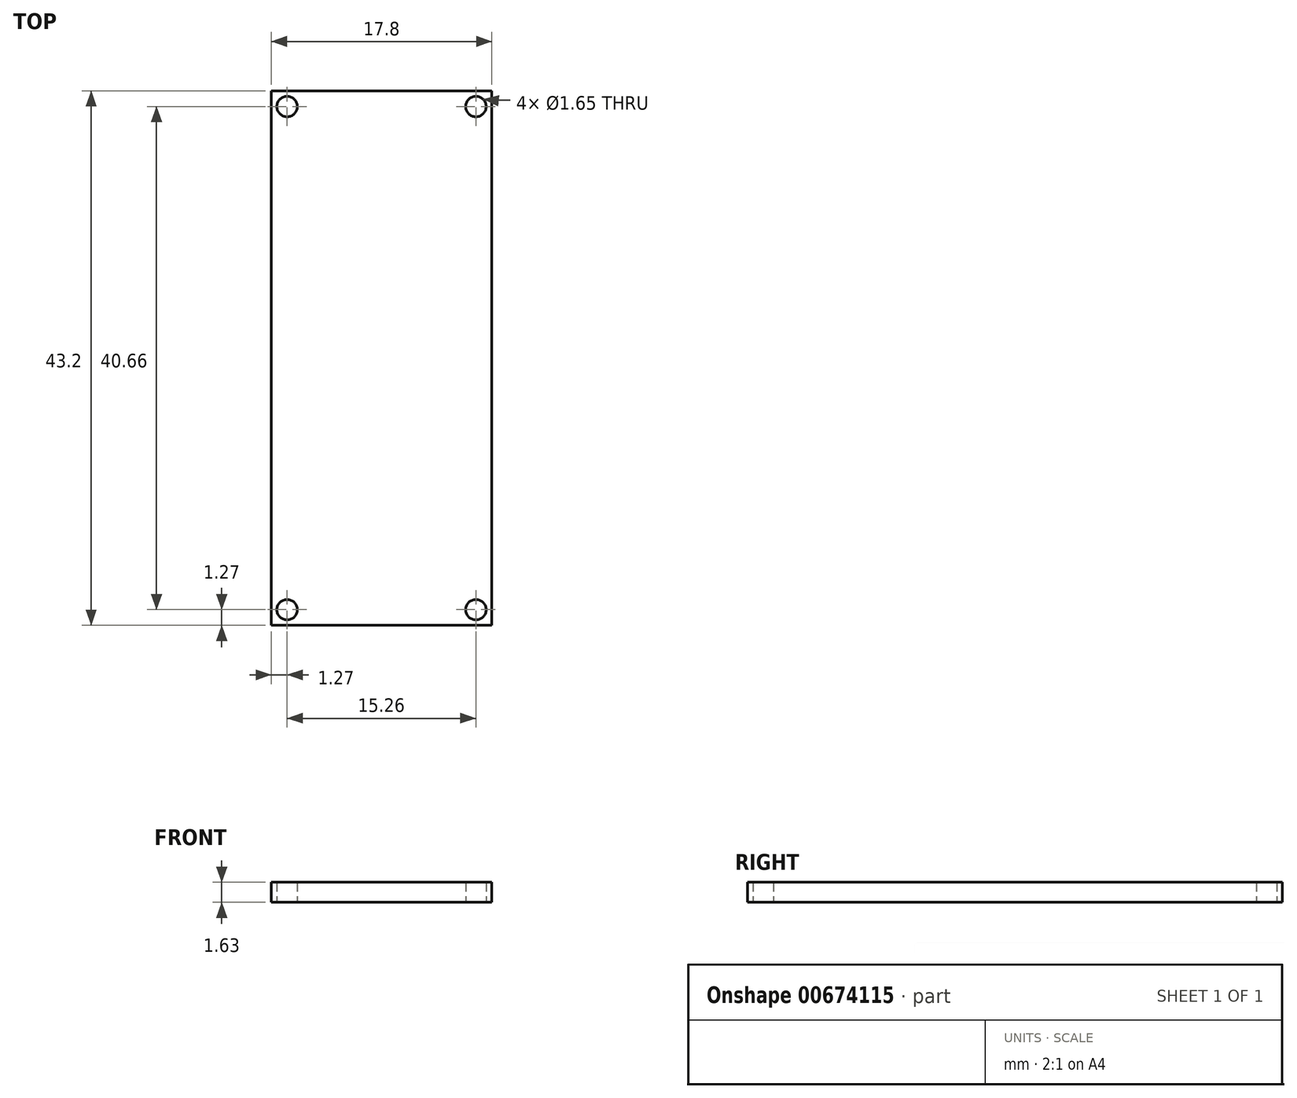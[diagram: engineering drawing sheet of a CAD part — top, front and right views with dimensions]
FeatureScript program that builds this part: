
annotation { "Feature Type Name" : "Feature", "Feature Type Description" : "" }
export const myFeature = defineFeature(function(context is Context, id is Id, definition is map)
    precondition{}
    {
        {
            var Q0;
            Q0=qCreatedBy(makeId("Top.planeOp"),FACE);
            var sketch = newSketch(context, id + "F0", { "sketchPlane" : qUnion([Q0])});
            skLineSegment(sketch, "E0.bottom", {"start": v(8.9, 21.6) * mm, "end": v(-8.9, 21.6) * mm});
            skLineSegment(sketch, "E0.top", {"start": v(8.9, -21.6) * mm, "end": v(-8.9, -21.6) * mm});
            skLineSegment(sketch, "E0.left", {"start": v(8.9, 21.6) * mm, "end": v(8.9, -21.6) * mm});
            skLineSegment(sketch, "E0.right", {"start": v(-8.9, 21.6) * mm, "end": v(-8.9, -21.6) * mm});
            skPoint(sketch, "E0.middle", {"position": v(0, 0) * mm});
            skCircle(sketch, "E1", {"center": v(-7.63, 20.33) * mm, "radius": 0.82 * mm});
            skCircle(sketch, "E2", {"center": v(7.63, 20.33) * mm, "radius": 0.82 * mm});
            skCircle(sketch, "E3", {"center": v(7.63, -20.33) * mm, "radius": 0.82 * mm});
            skCircle(sketch, "E4", {"center": v(-7.63, -20.33) * mm, "radius": 0.82 * mm});
            skSolve(sketch);
        }
        {
            var Q0;
            Q0 = qSketchRegion(id + "F0", true);
            extrude(context, id + "F1", {"entities" : qUnion([Q0]), "depth" : 1.63 * mm, "offsetDistance" : 25 * mm});
        }
    });
